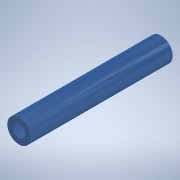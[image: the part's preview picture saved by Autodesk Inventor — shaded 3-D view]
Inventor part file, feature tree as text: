
AUTODESK INVENTOR PART (.ipt)
format: ipt  version: 2020 (Build 240168000, 168)  size: 105,984 bytes
history: native  units: in
note: dims shown in document units (in); Inventor stores cm internally (conversion verified against a paired STEP export)
features: extrude x1, sketch x1
ambient origin geometry x8: Origin, YZ Plane, XZ Plane, XY Plane, X Axis, Y Axis, Z Axis, Center Point
bodies: Solid1 (feature_tree)
feature tree (2):
  extrude  "Extrusion1"  Depth=2.27in
  sketch  "Sketch1"  dims[d0=0.203in d1=0.375in d2=2.27in d3=0.0in]
